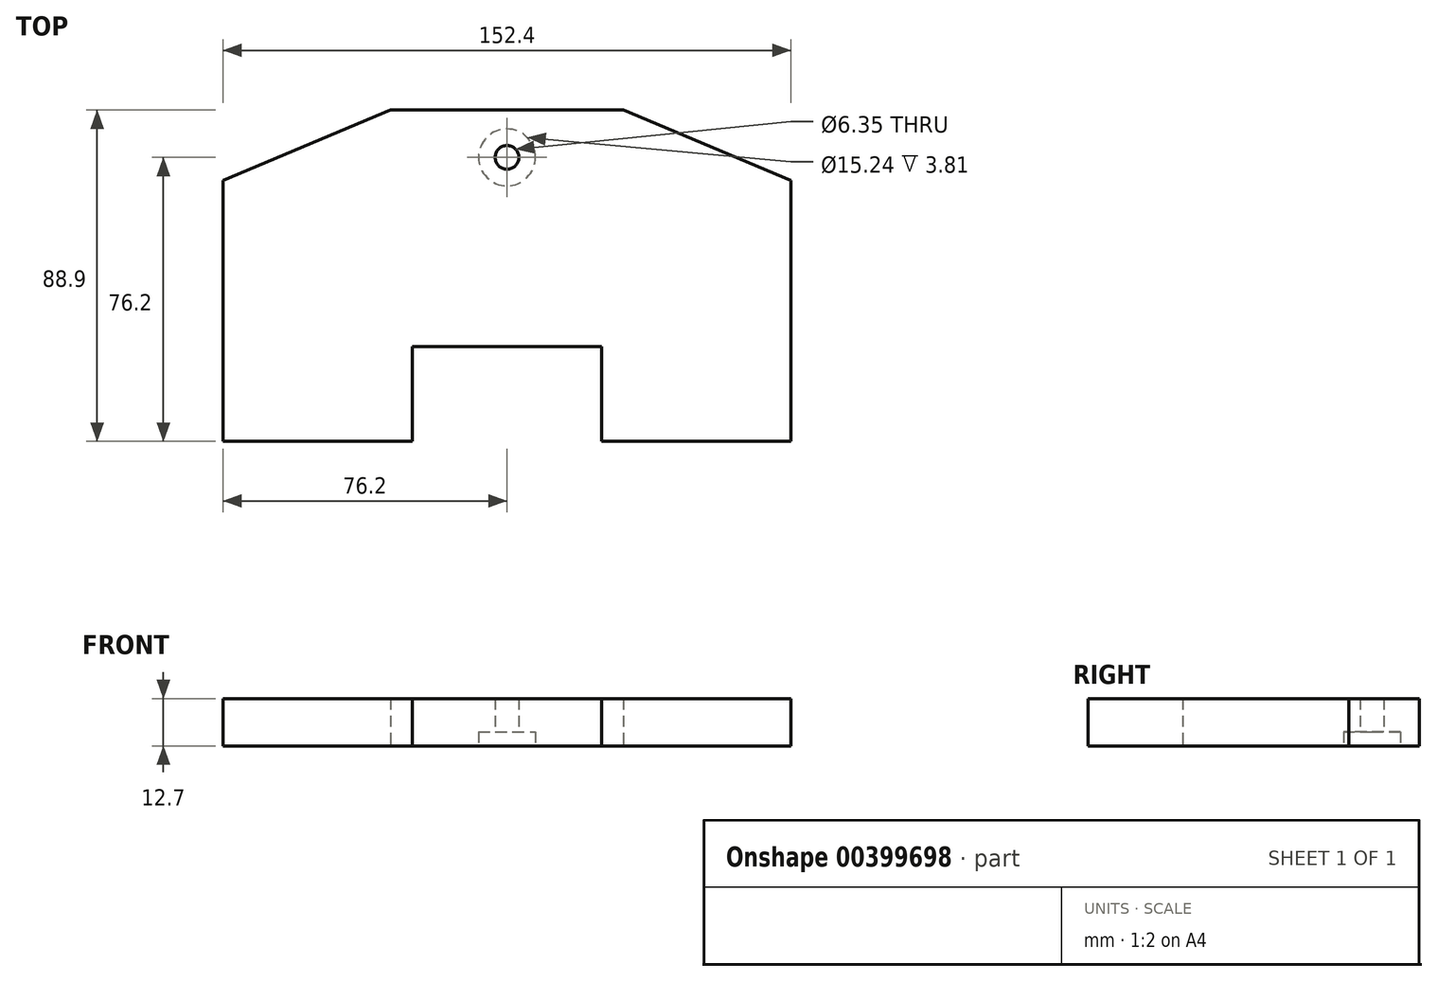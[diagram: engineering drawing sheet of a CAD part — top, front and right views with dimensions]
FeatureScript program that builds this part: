
annotation { "Feature Type Name" : "Feature", "Feature Type Description" : "" }
export const myFeature = defineFeature(function(context is Context, id is Id, definition is map)
    precondition{}
    {
        {
            var Q0;
            Q0=qCreatedBy(makeId("Top.planeOp"),FACE);
            var sketch = newSketch(context, id + "F0", { "sketchPlane" : qUnion([Q0])});
            skLineSegment(sketch, "E0.bottom", {"start": v(-76.2, 44.45) * mm, "end": v(76.2, 44.45) * mm});
            skLineSegment(sketch, "E0.top", {"start": v(-76.2, -44.45) * mm, "end": v(76.2, -44.45) * mm});
            skLineSegment(sketch, "E0.left", {"start": v(-76.2, 44.45) * mm, "end": v(-76.2, -44.45) * mm});
            skLineSegment(sketch, "E0.right", {"start": v(76.2, 44.45) * mm, "end": v(76.2, -44.45) * mm});
            skLineSegment(sketch, "E1", {"start": v(-76.2, 25.55) * mm, "end": v(-31.2, 44.45) * mm});
            skLineSegment(sketch, "E2", {"start": v(0, 44.45) * mm, "end": v(0, -44.45) * mm, "construction": true});
            skLineSegment(sketch, "E3.MirrorCS", {"start": v(76.2, 25.55) * mm, "end": v(31.2, 44.45) * mm});
            skLineSegment(sketch, "E4", {"start": v(-25.4, -44.45) * mm, "end": v(-25.4, -19.05) * mm});
            skLineSegment(sketch, "E5", {"start": v(-25.4, -19.05) * mm, "end": v(0, -19.05) * mm});
            skLineSegment(sketch, "E6.MirrorCS", {"start": v(25.4, -19.05) * mm, "end": v(0, -19.05) * mm});
            skLineSegment(sketch, "E7.MirrorCS", {"start": v(25.4, -44.45) * mm, "end": v(25.4, -19.05) * mm});
            skSolve(sketch);
        }
        {
            var Q0;
            {var subQ1=sQuery(id+"F0.wireOp",EDGE,"E0.top");Q0=makeQuery(id+"F0.imprint","IMPRINT",FACE,{"disambiguationData":[TD([[makeQuery(id+"F0.imprint","IMPRINT",EDGE,{"derivedFrom":subQ1}),1.0]])]});}
            extrude(context, id + "F1", {"entities" : qUnion([Q0]), "depth" : 12.7 * mm});
        }
        {
            var Q0;
            Q0=makeQuery(id+"F1.opExtrude","CAP_FACE",FACE,{"disambiguationData":[OSD([sQuery(id+"F0.wireOp",EDGE,"E0.bottom"),sQuery(id+"F0.wireOp",EDGE,"E0.top"),sQuery(id+"F0.wireOp",EDGE,"E0.left"),sQuery(id+"F0.wireOp",EDGE,"E0.right"),sQuery(id+"F0.wireOp",EDGE,"E1"),sQuery(id+"F0.wireOp",EDGE,"E3.MirrorCS"),sQuery(id+"F0.wireOp",EDGE,"E4"),sQuery(id+"F0.wireOp",EDGE,"E5"),sQuery(id+"F0.wireOp",EDGE,"E6.MirrorCS"),sQuery(id+"F0.wireOp",EDGE,"E7.MirrorCS")])],"isStart":true});
            var sketch = newSketch(context, id + "F2", { "sketchPlane" : qUnion([Q0])});
            skLineSegment(sketch, "E8", {"start": v(0, 19.05) * mm, "end": v(0, -44.45) * mm, "construction": true});
            skPoint(sketch, "E9", {"position": v(0, -31.75) * mm});
            skSolve(sketch);
        }
        {
            var Q0;
            Q0=sQuery(id+"F2.wireOp",VERTEX,"E9");
            var Q1;
            Q1=makeQuery(id+"F1.opExtrude","SWEPT_BODY",BODY,{"disambiguationData":[OSD([sQuery(id+"F0.wireOp",EDGE,"E0.bottom"),sQuery(id+"F0.wireOp",EDGE,"E0.top"),sQuery(id+"F0.wireOp",EDGE,"E0.left"),sQuery(id+"F0.wireOp",EDGE,"E0.right"),sQuery(id+"F0.wireOp",EDGE,"E1"),sQuery(id+"F0.wireOp",EDGE,"E3.MirrorCS"),sQuery(id+"F0.wireOp",EDGE,"E4"),sQuery(id+"F0.wireOp",EDGE,"E5"),sQuery(id+"F0.wireOp",EDGE,"E6.MirrorCS"),sQuery(id+"F0.wireOp",EDGE,"E7.MirrorCS")])]});
            hole(context, id + "F3", {"style" : HoleStyle.C_BORE, "endStyle" : HoleEndStyle.THROUGH, "holeDiameter" : 6.35 * mm, "cBoreDiameter" : 15.24 * mm, "cBoreDepth" : 3.8 * mm, "isTappedThrough" : true, "tappedDepth" : 12.7 * mm, "tapClearance" : 3, "locations" : qUnion([Q0]), "scope" : qUnion([Q1])});
        }
    });
